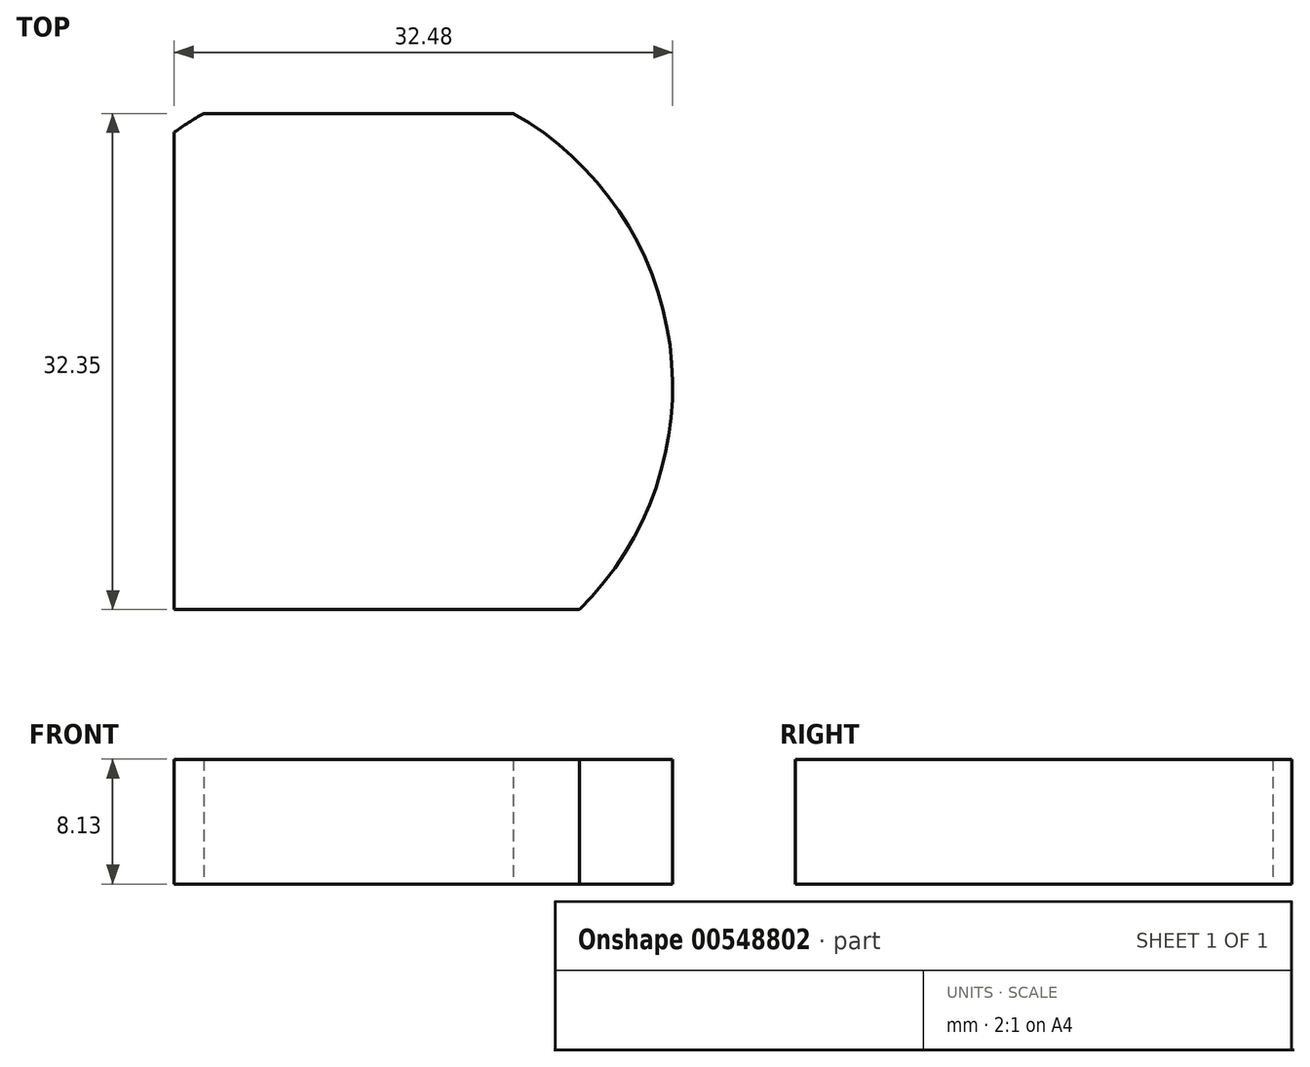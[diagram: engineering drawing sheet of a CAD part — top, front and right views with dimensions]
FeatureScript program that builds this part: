
annotation { "Feature Type Name" : "Feature", "Feature Type Description" : "" }
export const myFeature = defineFeature(function(context is Context, id is Id, definition is map)
    precondition{}
    {
        {
            var Q0;
            Q0=qCreatedBy(makeId("Top.planeOp"),FACE);
            var sketch = newSketch(context, id + "F0", { "sketchPlane" : qUnion([Q0])});
            skLineSegment(sketch, "E0.bottom", {"start": v(-56.6, 7.64) * mm, "end": v(66.46, 7.64) * mm});
            skLineSegment(sketch, "E0.top", {"start": v(-56.6, -24.7) * mm, "end": v(66.46, -24.7) * mm});
            skLineSegment(sketch, "E0.left", {"start": v(-56.6, 7.64) * mm, "end": v(-56.6, -24.7) * mm});
            skLineSegment(sketch, "E0.right", {"start": v(66.46, 7.64) * mm, "end": v(66.46, -24.7) * mm});
            skCircle(sketch, "E1", {"center": v(-44.6, -10.16) * mm, "radius": 20.46 * mm});
            skCircle(sketch, "E2", {"center": v(55.87, -8.07) * mm, "radius": 19.24 * mm});
            skSolve(sketch);
        }
        {
            var Q0;
            {var subQ0=sQuery(id+"F0.wireOp",EDGE,"E1");var subQ1=sQuery(id+"F0.wireOp",EDGE,"E0.bottom");var subQ2=makeQuery(id+"F0.imprint","INTERSECT",VERTEX,{"disambiguationData":[OD(1.0)],"derivedFrom":[subQ1,subQ0]});Q0=makeQuery(id+"F0.imprint","IMPRINT",FACE,{"disambiguationData":[TD([[makeQuery(id+"F0.imprint","IMPRINT",EDGE,{"disambiguationData":[TD([[subQ2,-1.0]])],"derivedFrom":subQ1}),-1.0]])]});}
            extrude(context, id + "F1", {"entities" : qUnion([Q0]), "depth" : 8.13 * mm, "offsetDistance" : 25.4 * mm});
        }
    });
